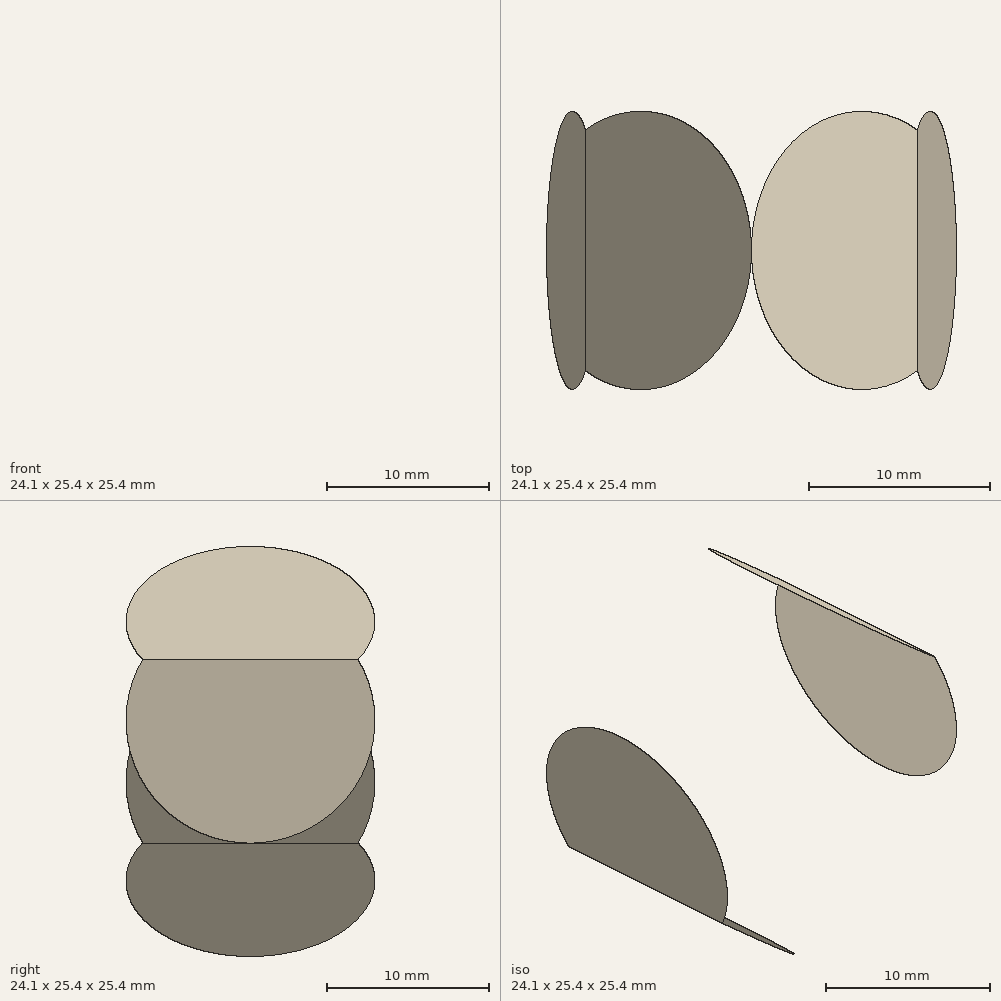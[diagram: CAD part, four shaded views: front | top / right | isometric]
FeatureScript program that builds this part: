
annotation { "Feature Type Name" : "Feature", "Feature Type Description" : "" }
export const myFeature = defineFeature(function(context is Context, id is Id, definition is map)
    precondition{}
    {
        {
            var Q0;
            Q0=qCreatedBy(makeId("Front.planeOp"),FACE);
            var sketch = newSketch(context, id + "F0", { "sketchPlane" : qUnion([Q0])});
            skArc(sketch, "E0", {"start": v(0, -12.7) * mm, "mid": v(12.7, 0) * mm, "end": v(0, 12.7) * mm});
            skLineSegment(sketch, "E1", {"start": v(0, 12.7) * mm, "end": v(0, -12.7) * mm});
            skLineSegment(sketch, "E2", {"start": v(0, -21.1) * mm, "end": v(0, 20.81) * mm, "construction": true});
            skLineSegment(sketch, "E3", {"start": v(0, 12.7) * mm, "end": v(12.25, 3.34) * mm});
            skLineSegment(sketch, "E4", {"start": v(0, -12.7) * mm, "end": v(-12.25, -3.34) * mm});
            skArc(sketch, "E5", {"start": v(-12.25, -3.34) * mm, "mid": v(-7.7, -10.1) * mm, "end": v(0, -12.7) * mm});
            skArc(sketch, "E6", {"start": v(0, -10.1) * mm, "mid": v(10.1, 0) * mm, "end": v(0, 10.1) * mm, "construction": true});
            skSolve(sketch);
        }
        {
            var Q0;
            {var subQ0=sQuery(id+"F0.wireOp",EDGE,"E1");Q0=makeQuery(id+"F0.imprint","IMPRINT",FACE,{"disambiguationData":[TD([[makeQuery(id+"F0.imprint","IMPRINT",EDGE,{"derivedFrom":subQ0}),1.0]])]});}
            var Q1;
            {var subQ0=sQuery(id+"F0.wireOp",EDGE,"E3");Q1=makeQuery(id+"F0.imprint","IMPRINT",FACE,{"disambiguationData":[TD([[makeQuery(id+"F0.imprint","IMPRINT",EDGE,{"derivedFrom":subQ0}),1.0]])]});}
            var Q2;
            {var subQ0=sQuery(id+"F0.wireOp",EDGE,"FxBFfuQ9-CBgf-wTTt-K6b3-vYgR4jaDMw1f");Q2=makeQuery(id+"F0.imprint","IMPRINT",FACE,{"disambiguationData":[TD([[makeQuery(id+"F0.imprint","IMPRINT",EDGE,{"derivedFrom":subQ0}),1.0]])]});}
            var Q3;
            Q3=sQuery(id+"F0.wireOp",EDGE,"E2");
            revolve(context, id + "F1", {"entities" : qUnion([Q0, Q1, Q2]), "axis" : qUnion([Q3]), "revolveType" : RevolveType.FULL});
        }
        {
            var Q0;
            {var subQ0=sQuery(id+"F0.wireOp",EDGE,"E3");Q0=makeQuery(id+"F0.imprint","IMPRINT",FACE,{"disambiguationData":[TD([[makeQuery(id+"F0.imprint","IMPRINT",EDGE,{"derivedFrom":subQ0}),1.0]])]});}
            extrude(context, id + "F2", {"entities" : qUnion([Q0]), "operationType" : NewBodyOperationType.REMOVE, "endBound" : BoundingType.THROUGH_ALL, "oppositeDirection" : true, "depth" : 12.7 * mm, "hasSecondDirection" : true, "secondDirectionBound" : SecondDirectionBoundingType.THROUGH_ALL, "secondDirectionOppositeDirection" : false, "secondDirectionDepth" : 12.7 * mm});
        }
        {
            var Q0;
            {var subQ0=sQuery(id+"F0.wireOp",EDGE,"E4");Q0=makeQuery(id+"F0.imprint","IMPRINT",FACE,{"disambiguationData":[TD([[makeQuery(id+"F0.imprint","IMPRINT",EDGE,{"derivedFrom":subQ0}),1.0]])]});}
            extrude(context, id + "F3", {"entities" : qUnion([Q0]), "operationType" : NewBodyOperationType.REMOVE, "oppositeDirection" : true, "depth" : 25.4 * mm, "hasSecondDirection" : true, "secondDirectionOppositeDirection" : false, "secondDirectionDepth" : 25.4 * mm});
        }
        {
            var Q0;
            Q0=qCreatedBy(makeId("Front.planeOp"),FACE);
            var sketch = newSketch(context, id + "F4", { "sketchPlane" : qUnion([Q0])});
            skLineSegment(sketch, "E7", {"start": v(7.9, 12.4) * mm, "end": v(12.6, -12.13) * mm});
            skLineSegment(sketch, "E8", {"start": v(12.6, -12.13) * mm, "end": v(16.59, -12.13) * mm});
            skLineSegment(sketch, "E9", {"start": v(16.59, -12.13) * mm, "end": v(16.59, 12.47) * mm});
            skLineSegment(sketch, "E10", {"start": v(16.59, 12.47) * mm, "end": v(7.9, 12.4) * mm});
            skLineSegment(sketch, "E11", {"start": v(-7.9, -12.47) * mm, "end": v(-12.6, 12.18) * mm});
            skLineSegment(sketch, "E12", {"start": v(-12.6, 12.18) * mm, "end": v(-15.2, 12.18) * mm});
            skLineSegment(sketch, "E13", {"start": v(-15.2, 12.18) * mm, "end": v(-15.2, -12.47) * mm});
            skLineSegment(sketch, "E14", {"start": v(-15.2, -12.47) * mm, "end": v(-7.9, -12.47) * mm});
            skSolve(sketch);
        }
        {
            var Q0;
            Q0=makeQuery(id+"F4.imprint","IMPRINT",FACE,{"disambiguationData":[TD([[makeQuery(id+"F4.imprint","IMPRINT",EDGE,{"derivedFrom":sQuery(id+"F4.wireOp",EDGE,"E7")}),1.0]])]});
            var Q1;
            Q1=makeQuery(id+"F4.imprint","IMPRINT",FACE,{"disambiguationData":[TD([[makeQuery(id+"F4.imprint","IMPRINT",EDGE,{"derivedFrom":sQuery(id+"F4.wireOp",EDGE,"E11")}),1.0]])]});
            extrude(context, id + "F5", {"entities" : qUnion([Q0, Q1]), "operationType" : NewBodyOperationType.REMOVE, "endBound" : BoundingType.THROUGH_ALL, "oppositeDirection" : true, "depth" : 25.4 * mm, "hasSecondDirection" : true, "secondDirectionBound" : SecondDirectionBoundingType.THROUGH_ALL, "secondDirectionOppositeDirection" : false, "secondDirectionDepth" : 25.4 * mm});
        }
    });
